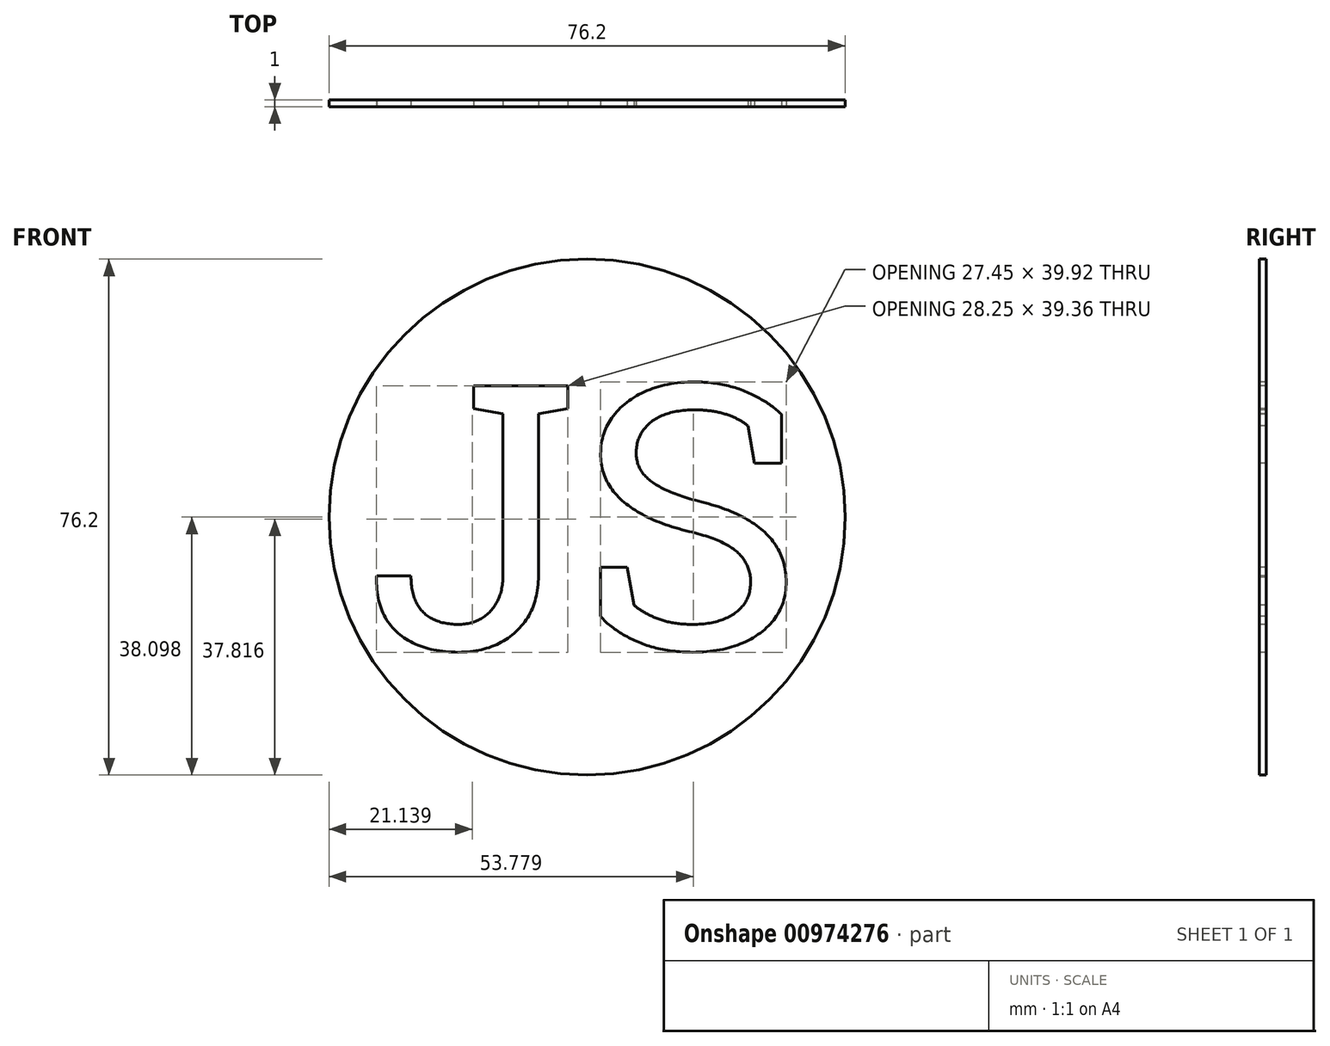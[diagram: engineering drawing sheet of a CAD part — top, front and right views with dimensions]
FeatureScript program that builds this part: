
annotation { "Feature Type Name" : "Feature", "Feature Type Description" : "" }
export const myFeature = defineFeature(function(context is Context, id is Id, definition is map)
    precondition{}
    {
        {
            var Q0;
            Q0=qCreatedBy(makeId("Front.planeOp"),FACE);
            var sketch = newSketch(context, id + "F0", { "sketchPlane" : qUnion([Q0])});
            skCircle(sketch, "E0", {"center": v(0, 0) * mm, "radius": 38.1 * mm});
            skSolve(sketch);
        }
        {
            var Q0;
            Q0 = qSketchRegion(id + "F0", true);
            extrude(context, id + "F1", {"entities" : qUnion([Q0]), "depth" : 1 * mm, "offsetDistance" : 25.4 * mm});
        }
        {
            var Q0;
            Q0=makeQuery(id+"F1.opExtrude","CAP_FACE",FACE,{"disambiguationData":[OSD([sQuery(id+"F0.wireOp",EDGE,"E0")])],"isStart":false});
            var sketch = newSketch(context, id + "F2", { "sketchPlane" : qUnion([Q0])});
            skText(sketch, "E1", { "text": "JS", "fontName": "RobotoSlab-Regular.ttf"});
            const initialGuessF2  = {"E1": [-0.03279, -0.0194, 1, 0, 0.03929]};
            skSetInitialGuess(sketch, initialGuessF2);
            skSolve(sketch);
        }
        {
            var Q0;
            Q0 = qSketchRegion(id + "F2", true);
            extrude(context, id + "F3", {"entities" : qUnion([Q0]), "operationType" : NewBodyOperationType.REMOVE, "oppositeDirection" : true, "depth" : 25.4 * mm, "offsetDistance" : 25.4 * mm});
        }
    });
